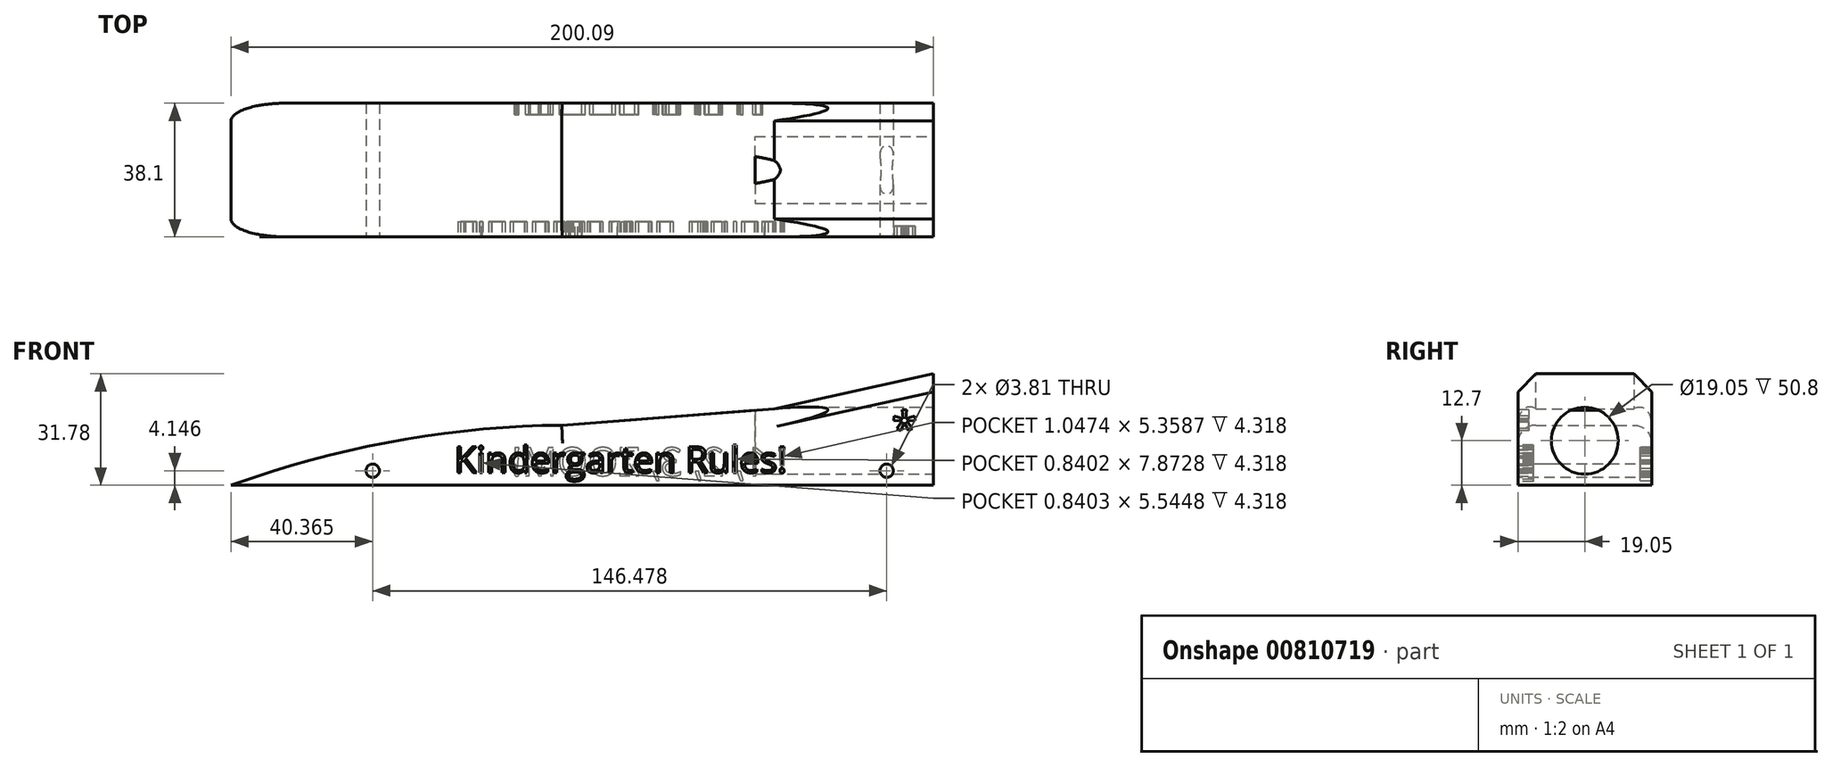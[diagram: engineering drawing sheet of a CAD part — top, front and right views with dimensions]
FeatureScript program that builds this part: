
annotation { "Feature Type Name" : "Feature", "Feature Type Description" : "" }
export const myFeature = defineFeature(function(context is Context, id is Id, definition is map)
    precondition{}
    {
        {
            var Q0;
            Q0=qCreatedBy(makeId("Front.planeOp"),FACE);
            var sketch = newSketch(context, id + "F0", { "sketchPlane" : qUnion([Q0])});
            skLineSegment(sketch, "E0", {"start": v(-124.2, 0) * mm, "end": v(-73.62, 17.14) * mm});
            skLineSegment(sketch, "E1", {"start": v(-73.62, 17.14) * mm, "end": v(-29.96, 17.14) * mm});
            skLineSegment(sketch, "E2", {"start": v(-29.96, 17.14) * mm, "end": v(30.57, 21.83) * mm});
            skLineSegment(sketch, "E3", {"start": v(30.57, 21.83) * mm, "end": v(75.9, 31.78) * mm});
            skLineSegment(sketch, "E4", {"start": v(75.9, 31.78) * mm, "end": v(75.9, 0) * mm});
            skLineSegment(sketch, "E5", {"start": v(75.9, 0) * mm, "end": v(-124.2, 0) * mm});
            skSolve(sketch);
        }
        {
            var Q0;
            Q0=makeQuery(id+"F0.imprint","IMPRINT",FACE,{"disambiguationData":[TD([[makeQuery(id+"F0.imprint","IMPRINT",EDGE,{"derivedFrom":sQuery(id+"F0.wireOp",EDGE,"E0")}),-1.0]])]});
            extrude(context, id + "F1", {"entities" : qUnion([Q0]), "depth" : 38.1 * mm, "offsetDistance" : 25.4 * mm});
        }
        {
            var Q0;
            Q0=makeQuery(id+"F1.opExtrude","SWEPT_EDGE",EDGE,{"disambiguationData":[OSD([sQuery(id+"F0.wireOp",EDGE,"E0"),sQuery(id+"F0.wireOp",EDGE,"E1")])]});
            fillet(context, id + "F2", {"entities" : qUnion([Q0]), "radius" : 282.47 * mm, "tangentPropagation" : true, "allowEdgeOverflow" : false});
        }
        {
            var Q0;
            Q0=makeQuery(id+"F1.opExtrude","CAP_FACE",FACE,{"disambiguationData":[OSD([sQuery(id+"F0.wireOp",EDGE,"E0"),sQuery(id+"F0.wireOp",EDGE,"E1"),sQuery(id+"F0.wireOp",EDGE,"E2"),sQuery(id+"F0.wireOp",EDGE,"E3"),sQuery(id+"F0.wireOp",EDGE,"E4"),sQuery(id+"F0.wireOp",EDGE,"E5")])],"isStart":false});
            var sketch = newSketch(context, id + "F3", { "sketchPlane" : qUnion([Q0])});
            skCircle(sketch, "E6", {"center": v(-83.83, 4.15) * mm, "radius": 1.9 * mm});
            skCircle(sketch, "E7", {"center": v(62.64, 4.15) * mm, "radius": 1.9 * mm});
            skSolve(sketch);
        }
        {
            var Q0;
            Q0=makeQuery(id+"F3.imprint","IMPRINT",FACE,{"disambiguationData":[TD([[makeQuery(id+"F3.imprint","IMPRINT",EDGE,{"derivedFrom":sQuery(id+"F3.wireOp",EDGE,"E6")}),1.0]])]});
            var Q1;
            Q1=sQuery(id+"F3.wireOp",EDGE,"E6");
            extrude(context, id + "F4", {"entities" : qUnion([Q0]), "operationType" : NewBodyOperationType.REMOVE, "surfaceEntities" : qUnion([Q1]), "oppositeDirection" : true, "depth" : 39.37 * mm, "offsetDistance" : 25.4 * mm});
        }
        {
            var Q0;
            Q0=makeQuery(id+"F3.imprint","IMPRINT",FACE,{"disambiguationData":[TD([[makeQuery(id+"F3.imprint","IMPRINT",EDGE,{"derivedFrom":sQuery(id+"F3.wireOp",EDGE,"E7")}),1.0]])]});
            var Q1;
            Q1=sQuery(id+"F3.wireOp",EDGE,"E7");
            extrude(context, id + "F5", {"entities" : qUnion([Q0]), "operationType" : NewBodyOperationType.REMOVE, "surfaceEntities" : qUnion([Q1]), "oppositeDirection" : true, "depth" : 54.1 * mm, "offsetDistance" : 25.4 * mm});
        }
        {
            var Q0;
            Q0=makeQuery(id+"F1.opExtrude","SWEPT_FACE",FACE,{"disambiguationData":[OSD([sQuery(id+"F0.wireOp",EDGE,"E4")])]});
            var sketch = newSketch(context, id + "F6", { "sketchPlane" : qUnion([Q0])});
            skCircle(sketch, "E8", {"center": v(-19.05, 12.7) * mm, "radius": 9.53 * mm});
            skSolve(sketch);
        }
        {
            var Q0;
            Q0=makeQuery(id+"F6.imprint","IMPRINT",FACE,{"disambiguationData":[TD([[makeQuery(id+"F6.imprint","IMPRINT",EDGE,{"derivedFrom":sQuery(id+"F6.wireOp",EDGE,"E8")}),1.0]])]});
            var Q1;
            Q1=sQuery(id+"F6.wireOp",EDGE,"E8");
            extrude(context, id + "F7", {"entities" : qUnion([Q0]), "operationType" : NewBodyOperationType.REMOVE, "surfaceEntities" : qUnion([Q1]), "oppositeDirection" : true, "depth" : 50.8 * mm, "offsetDistance" : 25.4 * mm});
        }
        {
            var Q0;
            {var subQ0=sQuery(id+"F0.wireOp",EDGE,"E1");var subQ1=sQuery(id+"F0.wireOp",EDGE,"E0");Q0=makeQuery(id+"F2.opFillet","BLEND_EDGE",EDGE,{"blendedFrom":[makeQuery(id+"F1.opExtrude","SWEPT_EDGE",EDGE,{"disambiguationData":[OSD([subQ1,subQ0])]}),makeQuery(id+"F1.opExtrude","CAP_FACE",FACE,{"disambiguationData":[OSD([subQ1,subQ0,sQuery(id+"F0.wireOp",EDGE,"E2"),sQuery(id+"F0.wireOp",EDGE,"E3"),sQuery(id+"F0.wireOp",EDGE,"E4"),sQuery(id+"F0.wireOp",EDGE,"E5")])],"isStart":true})],"blendedInto":[makeQuery(id+"F1.opExtrude","CAP_FACE",FACE,{"disambiguationData":[OSD([subQ1,subQ0,sQuery(id+"F0.wireOp",EDGE,"E2"),sQuery(id+"F0.wireOp",EDGE,"E3"),sQuery(id+"F0.wireOp",EDGE,"E4"),sQuery(id+"F0.wireOp",EDGE,"E5")])],"isStart":true})]});}
            var Q1;
            {var subQ0=sQuery(id+"F0.wireOp",EDGE,"E1");var subQ1=sQuery(id+"F0.wireOp",EDGE,"E0");Q1=makeQuery(id+"F2.opFillet","BLEND_EDGE",EDGE,{"blendedFrom":[makeQuery(id+"F1.opExtrude","SWEPT_EDGE",EDGE,{"disambiguationData":[OSD([subQ1,subQ0])]}),makeQuery(id+"F1.opExtrude","CAP_FACE",FACE,{"disambiguationData":[OSD([subQ1,subQ0,sQuery(id+"F0.wireOp",EDGE,"E2"),sQuery(id+"F0.wireOp",EDGE,"E3"),sQuery(id+"F0.wireOp",EDGE,"E4"),sQuery(id+"F0.wireOp",EDGE,"E5")])],"isStart":false})],"blendedInto":[makeQuery(id+"F1.opExtrude","CAP_FACE",FACE,{"disambiguationData":[OSD([subQ1,subQ0,sQuery(id+"F0.wireOp",EDGE,"E2"),sQuery(id+"F0.wireOp",EDGE,"E3"),sQuery(id+"F0.wireOp",EDGE,"E4"),sQuery(id+"F0.wireOp",EDGE,"E5")])],"isStart":false})]});}
            fillet(context, id + "F8", {"entities" : qUnion([Q0, Q1]), "radius" : 5.08 * mm, "tangentPropagation" : true, "allowEdgeOverflow" : false});
        }
        {
            var Q0;
            Q0=makeQuery(id+"F1.opExtrude","CAP_EDGE",EDGE,{"disambiguationData":[OSD([sQuery(id+"F0.wireOp",EDGE,"E3")])],"isStart":true});
            var Q1;
            Q1=makeQuery(id+"F1.opExtrude","CAP_EDGE",EDGE,{"disambiguationData":[OSD([sQuery(id+"F0.wireOp",EDGE,"E3")])],"isStart":false});
            chamfer(context, id + "F9", {"entities" : qUnion([Q0, Q1]), "width" : 5.08 * mm, "tangentPropagation" : true});
        }
        {
            var Q0;
            Q0=makeQuery(id+"F3.imprint","IMPRINT",FACE,{"disambiguationData":[TD([[makeQuery(id+"F3.imprint","IMPRINT",EDGE,{"derivedFrom":sQuery(id+"F3.wireOp",EDGE,"E6")}),-1.0]])]});
            var sketch = newSketch(context, id + "F10", { "sketchPlane" : qUnion([Q0])});
            skText(sketch, "E9", { "text": "Kindergarten Rules!", "fontName": "OpenSans-Regular.ttf"});
            const initialGuessF10  = {"E9": [-0.06062, 0.0036, 1, 0, 0.00746]};
            skSetInitialGuess(sketch, initialGuessF10);
            skSolve(sketch);
        }
        {
            var Q0;
            Q0 = qSketchRegion(id + "F10", true);
            extrude(context, id + "F11", {"entities" : qUnion([Q0]), "operationType" : NewBodyOperationType.REMOVE, "oppositeDirection" : true, "depth" : 4.32 * mm, "offsetDistance" : 25.4 * mm});
        }
        {
            var Q0;
            Q0=makeQuery(id+"F3.imprint","IMPRINT",FACE,{"disambiguationData":[TD([[makeQuery(id+"F3.imprint","IMPRINT",EDGE,{"derivedFrom":sQuery(id+"F3.wireOp",EDGE,"E6")}),-1.0]])]});
            var sketch = newSketch(context, id + "F12", { "sketchPlane" : qUnion([Q0])});
            skText(sketch, "E10", { "text": "*", "fontName": "OpenSans-Regular.ttf"});
            const initialGuessF12  = {"E10": [0.0641, 0.0115, 1, 0, 0.00949]};
            skSetInitialGuess(sketch, initialGuessF12);
            skSolve(sketch);
        }
        {
            var Q0;
            Q0 = qSketchRegion(id + "F12", true);
            extrude(context, id + "F13", {"entities" : qUnion([Q0]), "operationType" : NewBodyOperationType.REMOVE, "oppositeDirection" : true, "depth" : 3.05 * mm, "offsetDistance" : 25.4 * mm});
        }
        {
            var Q0;
            Q0=makeQuery(id+"F1.opExtrude","CAP_FACE",FACE,{"disambiguationData":[OSD([sQuery(id+"F0.wireOp",EDGE,"E0"),sQuery(id+"F0.wireOp",EDGE,"E1"),sQuery(id+"F0.wireOp",EDGE,"E2"),sQuery(id+"F0.wireOp",EDGE,"E3"),sQuery(id+"F0.wireOp",EDGE,"E4"),sQuery(id+"F0.wireOp",EDGE,"E5")])],"isStart":true});
            var sketch = newSketch(context, id + "F14", { "sketchPlane" : qUnion([Q0])});
            skText(sketch, "E11", { "text": "1, 2, 3, ZOOM!", "fontName": "OpenSans-Regular.ttf"});
            const initialGuessF14  = {"E11": [-0.02837, 0.00276, 1, 0, 0.00801]};
            skSetInitialGuess(sketch, initialGuessF14);
            skSolve(sketch);
        }
        {
            var Q0;
            Q0 = qSketchRegion(id + "F14", true);
            extrude(context, id + "F15", {"entities" : qUnion([Q0]), "operationType" : NewBodyOperationType.REMOVE, "oppositeDirection" : true, "depth" : 3.3 * mm, "offsetDistance" : 25.4 * mm});
        }
    });
